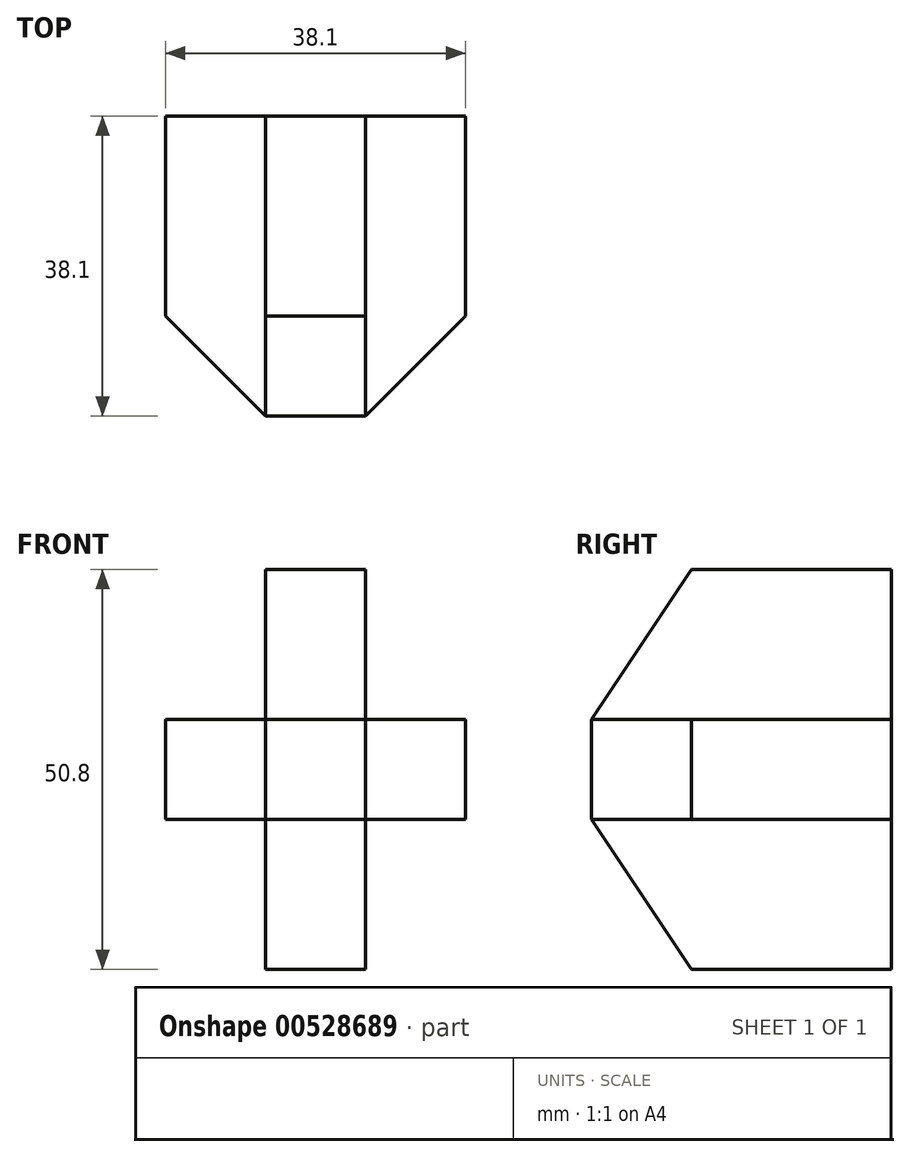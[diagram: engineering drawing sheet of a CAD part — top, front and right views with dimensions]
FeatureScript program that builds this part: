
annotation { "Feature Type Name" : "Feature", "Feature Type Description" : "" }
export const myFeature = defineFeature(function(context is Context, id is Id, definition is map)
    precondition{}
    {
        {
            var Q0;
            Q0=qCreatedBy(makeId("Front.planeOp"),FACE);
            var sketch = newSketch(context, id + "F0", { "sketchPlane" : qUnion([Q0])});
            skLineSegment(sketch, "E0", {"start": v(0, 0) * mm, "end": v(12.7, 0) * mm});
            skLineSegment(sketch, "E1", {"start": v(12.7, 0) * mm, "end": v(12.7, 31.75) * mm});
            skLineSegment(sketch, "E2", {"start": v(0, 0) * mm, "end": v(0, 31.75) * mm});
            skLineSegment(sketch, "E3", {"start": v(0, 31.75) * mm, "end": v(12.7, 31.75) * mm});
            skLineSegment(sketch, "E4", {"start": v(0, 0) * mm, "end": v(-12.7, 0) * mm});
            skLineSegment(sketch, "E5", {"start": v(-12.7, 0) * mm, "end": v(-12.7, 12.7) * mm});
            skLineSegment(sketch, "E6", {"start": v(-12.7, 12.7) * mm, "end": v(0, 12.7) * mm});
            skLineSegment(sketch, "E7", {"start": v(12.7, 0) * mm, "end": v(25.4, 0) * mm});
            skLineSegment(sketch, "E8", {"start": v(25.4, 0) * mm, "end": v(25.4, 12.7) * mm});
            skLineSegment(sketch, "E9", {"start": v(25.4, 12.7) * mm, "end": v(12.7, 12.7) * mm});
            skPoint(sketch, "E10.start.orphan", {"position": v(0, -1.93) * mm});
            skLineSegment(sketch, "E11", {"start": v(0, 0) * mm, "end": v(0, -19.05) * mm});
            skLineSegment(sketch, "E12", {"start": v(0, -19.05) * mm, "end": v(12.7, -19.05) * mm});
            skLineSegment(sketch, "E13", {"start": v(12.7, -19.05) * mm, "end": v(12.7, 0) * mm});
            skLineSegment(sketch, "E14", {"start": v(0, 12.7) * mm, "end": v(12.7, 12.7) * mm});
            skSolve(sketch);
        }
        {
            var Q0;
            {var subQ0=sQuery(id+"F0.wireOp",EDGE,"E4");Q0=makeQuery(id+"F0.imprint","IMPRINT",FACE,{"disambiguationData":[TD([[makeQuery(id+"F0.imprint","IMPRINT",EDGE,{"derivedFrom":subQ0}),-1.0]])]});}
            extrude(context, id + "F1", {"entities" : qUnion([Q0]), "depth" : 38.1 * mm, "offsetDistance" : 25.4 * mm});
        }
        {
            var Q0;
            Q0 = qSketchRegion(id + "F0", true);
            extrude(context, id + "F2", {"entities" : qUnion([Q0]), "operationType" : NewBodyOperationType.ADD, "depth" : 38.1 * mm, "offsetDistance" : 25.4 * mm});
        }
        {
            var Q0;
            Q0=makeQuery(id+"F1.opExtrude","SWEPT_FACE",FACE,{"disambiguationData":[OSD([sQuery(id+"F0.wireOp",EDGE,"E6")])]});
            var sketch = newSketch(context, id + "F3", { "sketchPlane" : qUnion([Q0])});
            skLineSegment(sketch, "E15", {"start": v(-12.7, -25.4) * mm, "end": v(0, -38.1) * mm});
            skLineSegment(sketch, "E16", {"start": v(-12.7, -25.4) * mm, "end": v(-12.7, -38.1) * mm});
            skLineSegment(sketch, "E17", {"start": v(-12.7, -38.19) * mm, "end": v(0, -38.1) * mm});
            skSolve(sketch);
        }
        {
            var Q0;
            Q0=makeQuery(id+"F3.imprint","IMPRINT",FACE,{"disambiguationData":[TD([[makeQuery(id+"F3.imprint","IMPRINT",EDGE,{"derivedFrom":sQuery(id+"F3.wireOp",EDGE,"E15")}),-1.0]])]});
            extrude(context, id + "F4", {"entities" : qUnion([Q0]), "operationType" : NewBodyOperationType.REMOVE, "oppositeDirection" : true, "depth" : 12.7 * mm, "offsetDistance" : 25.4 * mm});
        }
        {
            var Q0;
            Q0=makeQuery(id+"F2.opExtrude","SWEPT_FACE",FACE,{"disambiguationData":[OSD([sQuery(id+"F0.wireOp",EDGE,"E9")])]});
            var sketch = newSketch(context, id + "F5", { "sketchPlane" : qUnion([Q0])});
            skLineSegment(sketch, "E18", {"start": v(12.7, -38.1) * mm, "end": v(25.4, -38.1) * mm});
            skLineSegment(sketch, "E19", {"start": v(25.4, -38.1) * mm, "end": v(25.4, -25.4) * mm});
            skLineSegment(sketch, "E20", {"start": v(12.7, -38.1) * mm, "end": v(25.4, -25.4) * mm});
            skSolve(sketch);
        }
        {
            var Q0;
            Q0=makeQuery(id+"F5.imprint","IMPRINT",FACE,{"disambiguationData":[TD([[makeQuery(id+"F5.imprint","IMPRINT",EDGE,{"derivedFrom":sQuery(id+"F5.wireOp",EDGE,"E18")}),-1.0]])]});
            extrude(context, id + "F6", {"entities" : qUnion([Q0]), "operationType" : NewBodyOperationType.REMOVE, "oppositeDirection" : true, "depth" : 12.7 * mm, "offsetDistance" : 25.4 * mm});
        }
        {
            var Q0;
            Q0=makeQuery(id+"F2.opExtrude","SWEPT_FACE",FACE,{"disambiguationData":[OSD([sQuery(id+"F0.wireOp",EDGE,"E2")])]});
            var sketch = newSketch(context, id + "F7", { "sketchPlane" : qUnion([Q0])});
            skLineSegment(sketch, "E21", {"start": v(25.4, 31.75) * mm, "end": v(38.1, 31.75) * mm});
            skLineSegment(sketch, "E22", {"start": v(38.1, 31.75) * mm, "end": v(38.1, 12.7) * mm});
            skLineSegment(sketch, "E23", {"start": v(25.4, 31.75) * mm, "end": v(38.1, 12.7) * mm});
            skSolve(sketch);
        }
        {
            var Q0;
            Q0=makeQuery(id+"F7.imprint","IMPRINT",FACE,{"disambiguationData":[TD([[makeQuery(id+"F7.imprint","IMPRINT",EDGE,{"derivedFrom":sQuery(id+"F7.wireOp",EDGE,"E21")}),1.0]])]});
            extrude(context, id + "F8", {"entities" : qUnion([Q0]), "operationType" : NewBodyOperationType.REMOVE, "oppositeDirection" : true, "depth" : 12.7 * mm, "offsetDistance" : 25.4 * mm});
        }
        {
            var Q0;
            Q0=makeQuery(id+"F2.opExtrude","SWEPT_FACE",FACE,{"disambiguationData":[OSD([sQuery(id+"F0.wireOp",EDGE,"E11")])]});
            var sketch = newSketch(context, id + "F9", { "sketchPlane" : qUnion([Q0])});
            skLineSegment(sketch, "E24", {"start": v(25.38, 0) * mm, "end": v(38.1, 0) * mm});
            skLineSegment(sketch, "E25", {"start": v(38.1, 0) * mm, "end": v(38.1, -19.05) * mm});
            skLineSegment(sketch, "E26", {"start": v(25.4, -19.05) * mm, "end": v(38.1, -19.05) * mm});
            skLineSegment(sketch, "E27", {"start": v(25.4, -19.05) * mm, "end": v(38.1, 0) * mm});
            skSolve(sketch);
        }
        {
            var Q0;
            Q0=makeQuery(id+"F9.imprint","IMPRINT",FACE,{"disambiguationData":[TD([[makeQuery(id+"F9.imprint","IMPRINT",EDGE,{"derivedFrom":sQuery(id+"F9.wireOp",EDGE,"E25")}),-1.0]])]});
            extrude(context, id + "F10", {"entities" : qUnion([Q0]), "operationType" : NewBodyOperationType.REMOVE, "oppositeDirection" : true, "depth" : 12.7 * mm, "offsetDistance" : 25.4 * mm});
        }
    });
